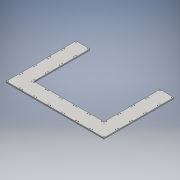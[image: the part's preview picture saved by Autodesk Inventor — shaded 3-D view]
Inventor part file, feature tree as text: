
AUTODESK INVENTOR PART (.ipt)
format: ipt  version: 2016 (Build 200138000, 138)  size: 283,136 bytes
history: native  units: mm
features: extrude x1
ambient origin geometry x8: Origin, YZ Plane, XZ Plane, XY Plane, X Axis, Y Axis, Z Axis, Center Point
bodies: Body1 (feature_tree)
feature tree (1):
  extrude  "Frame"  Depth=420.0mm
